# Revit family: SE-SU-410_GENERADO
name_source: partatom
category: Equipos especializados
units: mm (PartAtom-declared; Revit-internal decimal feet)

## family parameters
Compartido = No
Corte con vacíos al cargar = No
Cota de conector redondo = Diámetro de uso
Número OmniClass = 23.21.21.47
Punto de cálculo de habitación = No
Se basa en plano de trabajo = No
Siempre vertical = Sí
Tipo de pieza = Normal

## types (1)
- Vacuum packing machine SE-410  230/50-60/1
    Comentarios de tipo = Tabletop model. 10 m³/h. 420 mm
    Conn Plug = EU (SCHUKO 2P+G)
    Cycle = 50 Hz
    Depth = 529 mm  [stored 1.73556 ft]
    Descripción = Vacuum packing machine SE-410  230/50-60/1
    Elevación por defecto = 0 mm  [stored 0 ft]
    FL Amps = 3 A
    Fabricante = SAMMIC S.L.
    Foodservice Equipment Identifier = Sí
    Height = 413 mm  [stored 1.35499 ft]
    Modelo = 1140634
    Phase = 1
    Revision Code = 1
    Specification by Manufacturer = 420 mm sealing bar.

10 m³/h Busch vacuum pump.

Vacuum controlled by sensor.
    URL = https://www.sammic.com
    URL Cutsheet = http://www.sammic.com
    Volts = 230 V
    Weight in Pounds = 107.8
    Width = 484 mm  [stored 1.58793 ft]

note: [stored X ft] marks values corroborated as IEEE doubles in the binary element streams (Revit-internal decimal feet)
